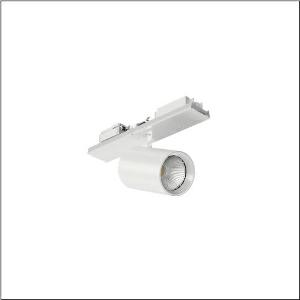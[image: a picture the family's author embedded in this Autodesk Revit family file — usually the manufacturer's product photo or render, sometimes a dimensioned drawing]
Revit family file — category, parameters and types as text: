
# Revit family: licross_spot_31_51sl12da45b
name_source: partatom
category: Lighting Fixtures
units: mm (PartAtom-declared; Revit-internal decimal feet)

## family parameters
Cut with Voids When Loaded = No
Host = Face
Light Source = No
Part Type = Normal
Room Calculation Point = No
Round Connector Dimension = Use Diameter
Shared = No

## types (1)
- --- (1 x LED, 5140 lm, 43.9 W, 4000K)
    Apparent Load = 44 VA
    CIE Flux Codes = 93 97 99 100 100
    Color Rendering = 90
    Color Temperature = 4000K
    Default Elevation = 1800 mm
    Description = Licross Spot 31, directional spotlight, light control with lens, of plastic, LED rated luminous flux: 5.140lm, light colour: 940, with plug, 5-pole, mains connection: 220..240V, AC, 50/60Hz, of aluminium, traffic white (RAL 9016), length: 300mm, diameter: 90mm, protection rating (complete): IP20, insulation class (complete): insulation class I (protective earthing), certification: CE, packaging unit: 1 piece
    Height = 175 mm
    Lamp = 1 x LED
    Lamp Light Flux = 5140 lm
    Lamp Power = 43.9 W
    Lamp count = 1
    Length = 90 mm
    Luminous efficacy = 117 lm/W
    Manufacturer = Siteco
    ModVariant = No
    Model = 51SL12DA45B
    Mounting Place = Ceiling
    Mounting Type = Pendant
    Number of Poles = 1
    OnlyDefault = Yes
    Power Factor = 1
    Product Name = Licross Spot 31
    Product group = directional spotlight
    ProductGroupID = 905
    Protection Class = Protection class I
    Protection Degree = IP 20
    RLX_Detail_Level = 1
    RLX_Emergency_Light_Flux = 0 lm
    RLX_Emergency_Type = 0
    RLX_Emergency_Type_DB = No
    RlxData = <blob elided: 14789 chars, md5=ba73fbda>
    Socket = socket
    Standby Power = 0 W
    System Light Flux = 5140 lm
    System Power = 44 W
    Type Comments = factory setting: luminous flux: 100 % | (ON | ON | ON) | 1050 mA
    Type Image = l_1245720.jpg
    URL = http://relux.com
    VarID = @adj_133613
    Voltage = 0 V
    Weight = 0.00 kg
    Width = 0 mm  [stored 0 ft]

note: [stored X ft] marks values corroborated as IEEE doubles in the binary element streams (Revit-internal decimal feet)

## geometry (parser evidence)
native form markers: Sweep x11
no freeform markers — native parametric forms only
